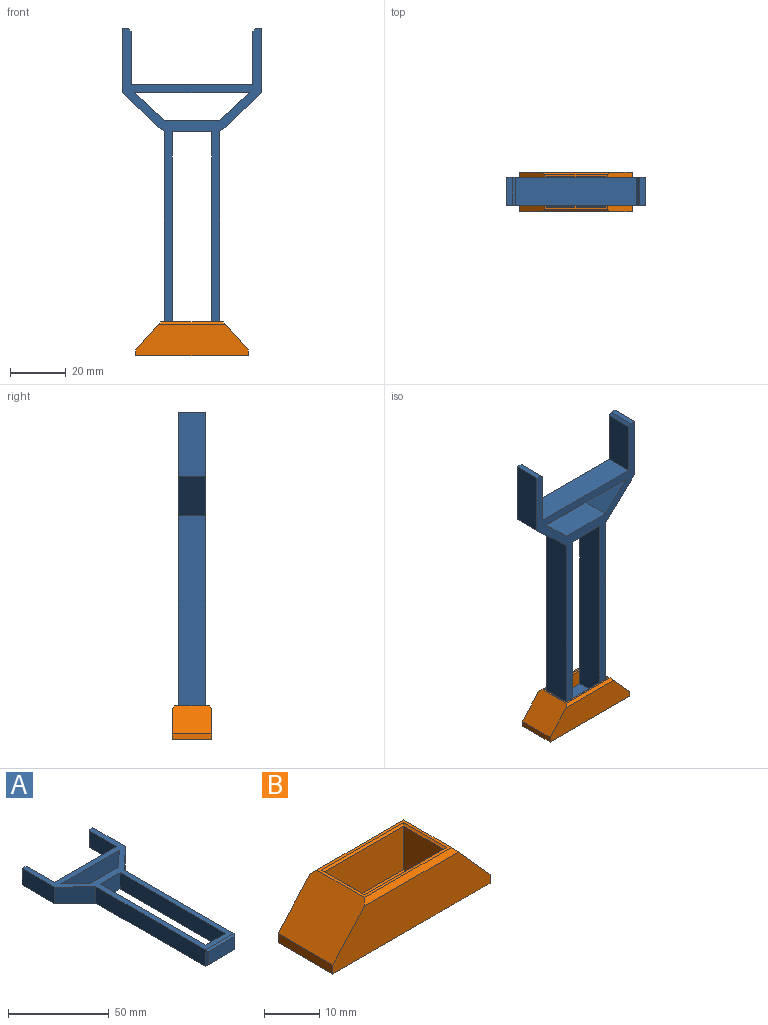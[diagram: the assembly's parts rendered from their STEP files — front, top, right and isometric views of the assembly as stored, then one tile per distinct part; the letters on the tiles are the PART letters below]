
ASSEMBLY  parts=2 mates=1
PART A: 28 faces, bbox 49.6x115x10 mm
  f0: plane 10.57x10mm, normal (0.69,0.73,0), area 145.5mm2, adj f1,f19,f20,f21
  f1: plane 40.87x10mm, normal (0,-1,0), area 408.7mm2, adj f0,f2,f20,f21
  f2: plane 10.57x10mm, normal (-0.69,0.73,0), area 145.5mm2, adj f1,f19,f20,f21
  f3: plane 14x10mm, normal (0,1,0), area 140mm2, adj f4,f17,f20,f21
  f4: plane 74x10mm, normal (1,0,0), area 740mm2, adj f3,f5,f20,f21
  f5: plane 14x10mm, normal (0,-1,0), area 140mm2, adj f4,f17,f20,f21
  f6: plane 10x2mm, normal (0,1,0), area 20mm2, adj f7,f20,f21,f22
  f7: plane 23x10mm, normal (-1,0,0), area 230mm2, adj f6,f8,f20,f21
  f8: plane 14.8x14mm, normal (-0.69,-0.73,0), area 203.7mm2, adj f7,f9,f20,f21
  f9: plane 77x10mm, normal (-1,0,0), area 770mm2, adj f8,f20,f21,f25
  f10: plane 18x8mm, normal (0,-1,0), area 144mm2, adj f24,f25,f26,f27
  f11: plane 77x10mm, normal (1,0,0), area 770mm2, adj f12,f20,f21,f26
  f12: plane 14.8x14mm, normal (0.69,-0.73,0), area 203.7mm2, adj f11,f13,f20,f21
  f13: plane 23x10mm, normal (1,0,0), area 230mm2, adj f12,f14,f20,f21
  f14: plane 10x2mm, normal (0,1,0), area 20mm2, adj f13,f20,f21,f23
  f15: plane 19x10mm, normal (-1,0,0), area 190mm2, adj f16,f20,f21,f23
  f16: plane 43.6x10mm, normal (0,1,0), area 436mm2, adj f15,f18,f20,f21
  f17: plane 74x10mm, normal (-1,0,0), area 740mm2, adj f3,f5,f20,f21
  f18: plane 19x10mm, normal (1,0,0), area 190mm2, adj f16,f20,f21,f22
  f19: plane 19.73x10mm, normal (0,1,0), area 197.3mm2, adj f0,f2,f20,f21
  f20: plane 114x49.6mm, normal (0,0,1), area 956mm2, adj f0,f1,f2,f3,f4,f5,f6,f7
  f21: plane 114x49.6mm, normal (0,0,-1), area 956mm2, adj f0,f1,f2,f3,f4,f5,f6,f7
  f22: plane 10x1mm, normal (0.71,0.71,0), area 14.1mm2, adj f6,f18,f20,f21
  f23: plane 10x1mm, normal (-0.71,0.71,0), area 14.1mm2, adj f14,f15,f20,f21
  f24: plane 20x1mm, normal (0,-0.71,0.71), area 26.9mm2, adj f10,f20,f25,f26
  f25: plane 10x1mm, normal (-0.71,-0.71,0), area 12.7mm2, adj f9,f10,f24,f27
  f26: plane 10x1mm, normal (0.71,-0.71,0), area 12.7mm2, adj f10,f11,f24,f27
  f27: plane 20x1mm, normal (0,-0.71,-0.71), area 26.9mm2, adj f10,f21,f25,f26
PART B: 19 faces, bbox 40.2x14x12 mm
  f0: plane 14x10mm, normal (-0.74,0,0.67), area 187.1mm2, adj f1,f3,f4,f11,f13,f14
  f1: plane 24x1mm, normal (0,0.74,0.67), area 31.1mm2, adj f0,f2,f3,f14
  f2: plane 14x10mm, normal (0.74,0,0.67), area 187.1mm2, adj f1,f3,f5,f11,f13,f14
  f3: plane 22.2x12.2mm, normal (0,0,1), area 39.8mm2, adj f0,f1,f2,f11,f15,f16,f17,f18
  f4: plane 14x2mm, normal (-1,0,0), area 28mm2, adj f0,f12,f13,f14
  f5: plane 14x2mm, normal (1,0,0), area 28mm2, adj f2,f12,f13,f14
  f6: plane 20.2x9.6mm, normal (0,-1,0), area 193.9mm2, adj f7,f9,f10,f15
  f7: plane 10.2x9.6mm, normal (1,0,0), area 97.9mm2, adj f6,f8,f10,f16
  f8: plane 20.2x9.6mm, normal (0,1,0), area 193.9mm2, adj f7,f9,f10,f18
  f9: plane 10.2x9.6mm, normal (-1,0,0), area 97.9mm2, adj f6,f8,f10,f17
  f10: plane 20.2x10.2mm, normal (0,0,1), area 206mm2, adj f6,f7,f8,f9
  f11: plane 24x1mm, normal (0,-0.74,0.67), area 31.1mm2, adj f0,f2,f3,f13
  f12: plane 40.2x14mm, normal (0,0,-1), area 562.8mm2, adj f4,f5,f13,f14
  f13: plane 40.2x11mm, normal (0,-1,0), area 369.3mm2, adj f0,f2,f4,f5,f11,f12
  f14: plane 40.2x11mm, normal (0,1,0), area 369.3mm2, adj f0,f1,f2,f4,f5,f12
  f15: plane 21x0.4mm, normal (0,-0.71,0.71), area 11.7mm2, adj f3,f6,f16,f17
  f16: plane 11x0.4mm, normal (0.71,0,0.71), area 6mm2, adj f3,f7,f15,f18
  f17: plane 11x0.4mm, normal (-0.71,0,0.71), area 6mm2, adj f3,f9,f15,f18
  f18: plane 21x0.4mm, normal (0,0.71,0.71), area 11.7mm2, adj f3,f8,f16,f17
PLACE A rot(axis=(1,0,0),90deg) t=(-6.51,3.29,-0.43)mm
PLACE B t=(-6.51,-1.71,-0.43)mm fixed
MATE fastened B.f10 <-> A.f10  axis (0,0,1) through (-6.51,-1.71,-0.43)mm
